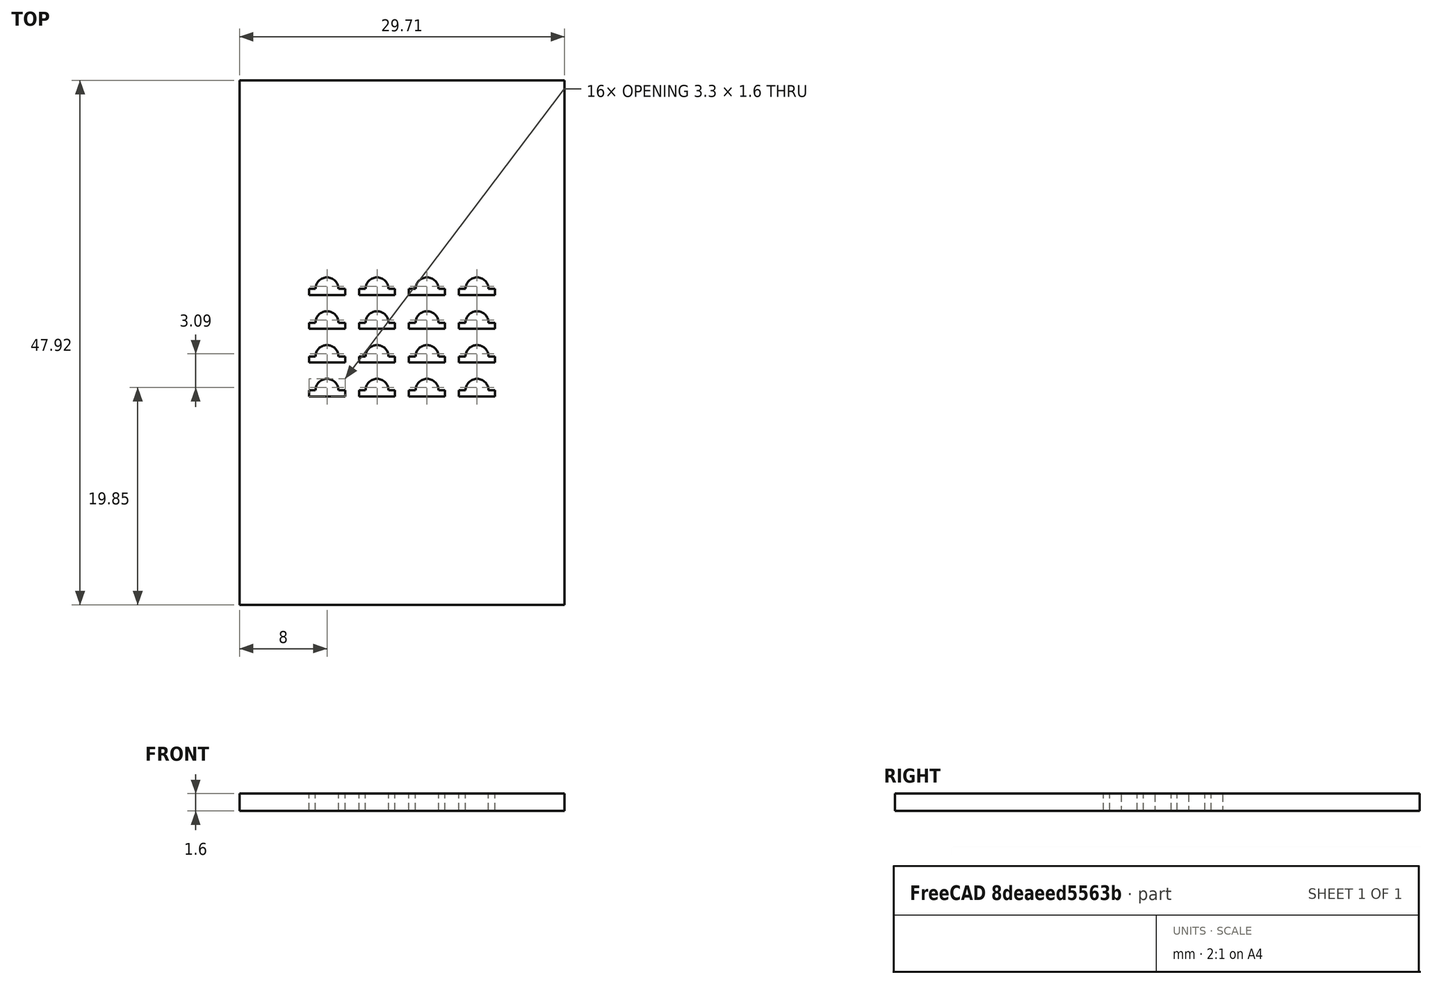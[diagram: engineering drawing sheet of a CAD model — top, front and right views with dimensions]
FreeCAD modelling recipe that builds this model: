
FCSTD DOCUMENT  (FreeCAD 0.18.1R)
Label: Board_Outline_Rev_01
License: All rights reserved
LicenseURL: http://en.wikipedia.org/wiki/All_rights_reserved
objects: Sketcher::SketchObject×1, PartDesign::Pad×1, PartDesign::Body×1, Mesh::Feature×1
note: 4 computed .brp shape members not serialized (recipe doc carries the construction recipe); baked Part::Feature solids carry a one-line shape summary decoded from their .brp

FEATURE [Sketcher::SketchObject] Sketch
  MapMode = 5
  Support = -> [XY_Plane]
  sketch-geometry (116):
    g0: LineSegment StartX=0 StartY=0 StartZ=0 EndX=1.65 EndY=0 EndZ=0
    g1: LineSegment StartX=0 StartY=0 StartZ=0 EndX=-1.65 EndY=0 EndZ=0
    g2: LineSegment StartX=-1.65 StartY=0 StartZ=0 EndX=-1.65 EndY=0.55 EndZ=0
    g3: LineSegment StartX=1.65 StartY=0 StartZ=0 EndX=1.65 EndY=0.55 EndZ=0
    g4: LineSegment StartX=-1.65 StartY=0.55 StartZ=0 EndX=-1.05 EndY=0.55 EndZ=0
    g5: LineSegment StartX=1.65 StartY=0.55 StartZ=0 EndX=1.05 EndY=0.55 EndZ=0
    g6: ArcOfCircle CenterX=0 CenterY=0.55 CenterZ=0 NormalX=0 NormalY=0 NormalZ=1 AngleXU=0 Radius=1.05 StartAngle=0 EndAngle=3.14159
    g7: LineSegment StartX=4.57 StartY=0 StartZ=0 EndX=6.22 EndY=0 EndZ=0
    g8: LineSegment StartX=4.57 StartY=0 StartZ=0 EndX=2.92 EndY=0 EndZ=0
    g9: LineSegment StartX=2.92 StartY=0 StartZ=0 EndX=2.92 EndY=0.55 EndZ=0
    g10: LineSegment StartX=6.22 StartY=0 StartZ=0 EndX=6.22 EndY=0.55 EndZ=0
    g11: LineSegment StartX=2.92 StartY=0.55 StartZ=0 EndX=3.52 EndY=0.55 EndZ=0
    g12: LineSegment StartX=6.22 StartY=0.55 StartZ=0 EndX=5.62 EndY=0.55 EndZ=0
    g13: ArcOfCircle CenterX=4.57 CenterY=0.55 CenterZ=0 NormalX=0 NormalY=0 NormalZ=1 AngleXU=0 Radius=1.05 StartAngle=0 EndAngle=3.14159
    g14: LineSegment StartX=9.14 StartY=0 StartZ=0 EndX=10.79 EndY=0 EndZ=0
    g15: LineSegment StartX=9.14 StartY=0 StartZ=0 EndX=7.49 EndY=0 EndZ=0
    g16: LineSegment StartX=7.49 StartY=0 StartZ=0 EndX=7.49 EndY=0.55 EndZ=0
    g17: LineSegment StartX=10.79 StartY=0 StartZ=0 EndX=10.79 EndY=0.55 EndZ=0
    g18: LineSegment StartX=7.49 StartY=0.55 StartZ=0 EndX=8.09 EndY=0.55 EndZ=0
    g19: LineSegment StartX=10.79 StartY=0.55 StartZ=0 EndX=10.19 EndY=0.55 EndZ=0
    g20: ArcOfCircle CenterX=9.14 CenterY=0.55 CenterZ=0 NormalX=0 NormalY=0 NormalZ=1 AngleXU=0 Radius=1.05 StartAngle=0 EndAngle=3.14159
    g21: LineSegment StartX=13.71 StartY=0 StartZ=0 EndX=15.36 EndY=0 EndZ=0
    g22: LineSegment StartX=13.71 StartY=0 StartZ=0 EndX=12.06 EndY=0 EndZ=0
    g23: LineSegment StartX=12.06 StartY=0 StartZ=0 EndX=12.06 EndY=0.55 EndZ=0
    g24: LineSegment StartX=15.36 StartY=0 StartZ=0 EndX=15.36 EndY=0.55 EndZ=0
    g25: LineSegment StartX=12.06 StartY=0.55 StartZ=0 EndX=12.66 EndY=0.55 EndZ=0
    g26: LineSegment StartX=15.36 StartY=0.55 StartZ=0 EndX=14.76 EndY=0.55 EndZ=0
    g27: ArcOfCircle CenterX=13.71 CenterY=0.55 CenterZ=0 NormalX=0 NormalY=0 NormalZ=1 AngleXU=0 Radius=1.05 StartAngle=0 EndAngle=3.14159
    g28: LineSegment StartX=1e-06 StartY=3.09 StartZ=0 EndX=1.65 EndY=3.09 EndZ=0
    g29: LineSegment StartX=1e-06 StartY=3.09 StartZ=0 EndX=-1.65 EndY=3.09 EndZ=0
    g30: LineSegment StartX=-1.65 StartY=3.09 StartZ=0 EndX=-1.65 EndY=3.64 EndZ=0
    g31: LineSegment StartX=1.65 StartY=3.09 StartZ=0 EndX=1.65 EndY=3.64 EndZ=0
    g32: LineSegment StartX=-1.65 StartY=3.64 StartZ=0 EndX=-1.05 EndY=3.64 EndZ=0
    g33: LineSegment StartX=1.65 StartY=3.64 StartZ=0 EndX=1.05 EndY=3.64 EndZ=0
    g34: ArcOfCircle CenterX=0 CenterY=3.64 CenterZ=0 NormalX=0 NormalY=0 NormalZ=1 AngleXU=0 Radius=1.05 StartAngle=3e-16 EndAngle=3.14159
    g35: LineSegment StartX=4.57 StartY=3.09 StartZ=0 EndX=6.22 EndY=3.09 EndZ=0
    g36: LineSegment StartX=4.57 StartY=3.09 StartZ=0 EndX=2.92 EndY=3.09 EndZ=0
    g37: LineSegment StartX=2.92 StartY=3.09 StartZ=0 EndX=2.92 EndY=3.64 EndZ=0
    g38: LineSegment StartX=6.22 StartY=3.09 StartZ=0 EndX=6.22 EndY=3.64 EndZ=0
    g39: LineSegment StartX=2.92 StartY=3.64 StartZ=0 EndX=3.52 EndY=3.64 EndZ=0
    g40: LineSegment StartX=6.22 StartY=3.64 StartZ=0 EndX=5.62 EndY=3.64 EndZ=0
    g41: ArcOfCircle CenterX=4.57 CenterY=3.64 CenterZ=0 NormalX=0 NormalY=0 NormalZ=1 AngleXU=0 Radius=1.05 StartAngle=1.4e-15 EndAngle=3.14159
    g42: LineSegment StartX=9.14 StartY=3.09 StartZ=0 EndX=10.79 EndY=3.09 EndZ=0
    g43: LineSegment StartX=9.14 StartY=3.09 StartZ=0 EndX=7.49 EndY=3.09 EndZ=0
    g44: LineSegment StartX=7.49 StartY=3.09 StartZ=0 EndX=7.49 EndY=3.64 EndZ=0
    g45: LineSegment StartX=10.79 StartY=3.09 StartZ=0 EndX=10.79 EndY=3.64 EndZ=0
    g46: LineSegment StartX=7.49 StartY=3.64 StartZ=0 EndX=8.09 EndY=3.64 EndZ=0
    g47: LineSegment StartX=10.79 StartY=3.64 StartZ=0 EndX=10.19 EndY=3.64 EndZ=0
    g48: ArcOfCircle CenterX=9.14 CenterY=3.64 CenterZ=0 NormalX=0 NormalY=0 NormalZ=1 AngleXU=0 Radius=1.05 StartAngle=0 EndAngle=3.14159
    g49: LineSegment StartX=13.71 StartY=3.09 StartZ=0 EndX=15.36 EndY=3.09 EndZ=0
    g50: LineSegment StartX=13.71 StartY=3.09 StartZ=0 EndX=12.06 EndY=3.09 EndZ=0
    g51: LineSegment StartX=12.06 StartY=3.09 StartZ=0 EndX=12.06 EndY=3.64 EndZ=0
    g52: LineSegment StartX=15.36 StartY=3.09 StartZ=0 EndX=15.36 EndY=3.64 EndZ=0
    g53: LineSegment StartX=12.06 StartY=3.64 StartZ=0 EndX=12.66 EndY=3.64 EndZ=0
    g54: LineSegment StartX=15.36 StartY=3.64 StartZ=0 EndX=14.76 EndY=3.64 EndZ=0
    g55: ArcOfCircle CenterX=13.71 CenterY=3.64 CenterZ=0 NormalX=0 NormalY=0 NormalZ=1 AngleXU=0 Radius=1.05 StartAngle=5.7e-15 EndAngle=3.14159
    g56: LineSegment StartX=0 StartY=6.18 StartZ=0 EndX=1.65 EndY=6.18 EndZ=0
    g57: LineSegment StartX=0 StartY=6.18 StartZ=0 EndX=-1.65 EndY=6.18 EndZ=0
    g58: LineSegment StartX=-1.65 StartY=6.18 StartZ=0 EndX=-1.65 EndY=6.73 EndZ=0
    g59: LineSegment StartX=1.65 StartY=6.18 StartZ=0 EndX=1.65 EndY=6.73 EndZ=0
    g60: LineSegment StartX=-1.65 StartY=6.73 StartZ=0 EndX=-1.05 EndY=6.73 EndZ=0
    g61: LineSegment StartX=1.65 StartY=6.73 StartZ=0 EndX=1.05 EndY=6.73 EndZ=0
    g62: ArcOfCircle CenterX=0 CenterY=6.73 CenterZ=0 NormalX=0 NormalY=0 NormalZ=1 AngleXU=0 Radius=1.05 StartAngle=7e-16 EndAngle=3.14159
    g63: LineSegment StartX=4.57 StartY=6.18 StartZ=0 EndX=6.22 EndY=6.18 EndZ=0
    g64: LineSegment StartX=4.57 StartY=6.18 StartZ=0 EndX=2.92 EndY=6.18 EndZ=0
    g65: LineSegment StartX=2.92 StartY=6.18 StartZ=0 EndX=2.92 EndY=6.73 EndZ=0
    g66: LineSegment StartX=6.22 StartY=6.18 StartZ=0 EndX=6.22 EndY=6.73 EndZ=0
    g67: LineSegment StartX=2.92 StartY=6.73 StartZ=0 EndX=3.52 EndY=6.73 EndZ=0
    g68: LineSegment StartX=6.22 StartY=6.73 StartZ=0 EndX=5.62 EndY=6.73 EndZ=0
    g69: ArcOfCircle CenterX=4.57 CenterY=6.73 CenterZ=0 NormalX=0 NormalY=0 NormalZ=1 AngleXU=0 Radius=1.05 StartAngle=-9e-16 EndAngle=3.14159
    g70: LineSegment StartX=9.14 StartY=6.18 StartZ=0 EndX=10.79 EndY=6.18 EndZ=0
    g71: LineSegment StartX=9.14 StartY=6.18 StartZ=0 EndX=7.49 EndY=6.18 EndZ=0
    g72: LineSegment StartX=7.49 StartY=6.18 StartZ=0 EndX=7.49 EndY=6.73 EndZ=0
    g73: LineSegment StartX=10.79 StartY=6.18 StartZ=0 EndX=10.79 EndY=6.73 EndZ=0
    g74: LineSegment StartX=7.49 StartY=6.73 StartZ=0 EndX=8.09 EndY=6.73 EndZ=0
    g75: LineSegment StartX=10.79 StartY=6.73 StartZ=0 EndX=10.19 EndY=6.73 EndZ=0
    g76: ArcOfCircle CenterX=9.14 CenterY=6.73 CenterZ=0 NormalX=0 NormalY=0 NormalZ=1 AngleXU=0 Radius=1.05 StartAngle=4.3e-15 EndAngle=3.14159
    g77: LineSegment StartX=13.71 StartY=6.18 StartZ=0 EndX=15.36 EndY=6.18 EndZ=0
    g78: LineSegment StartX=13.71 StartY=6.18 StartZ=0 EndX=12.06 EndY=6.18 EndZ=0
    g79: LineSegment StartX=12.06 StartY=6.18 StartZ=0 EndX=12.06 EndY=6.73 EndZ=0
    g80: LineSegment StartX=15.36 StartY=6.18 StartZ=0 EndX=15.36 EndY=6.73 EndZ=0
    g81: LineSegment StartX=12.06 StartY=6.73 StartZ=0 EndX=12.66 EndY=6.73 EndZ=0
    g82: LineSegment StartX=15.36 StartY=6.73 StartZ=0 EndX=14.76 EndY=6.73 EndZ=0
    g83: ArcOfCircle CenterX=13.71 CenterY=6.73 CenterZ=0 NormalX=0 NormalY=0 NormalZ=1 AngleXU=0 Radius=1.05 StartAngle=1.2e-15 EndAngle=3.14159
    g84: LineSegment StartX=1e-06 StartY=9.27 StartZ=0 EndX=1.65 EndY=9.27 EndZ=0
    g85: LineSegment StartX=1e-06 StartY=9.27 StartZ=0 EndX=-1.65 EndY=9.27 EndZ=0
    g86: LineSegment StartX=-1.65 StartY=9.27 StartZ=0 EndX=-1.65 EndY=9.82 EndZ=0
    g87: LineSegment StartX=1.65 StartY=9.27 StartZ=0 EndX=1.65 EndY=9.82 EndZ=0
    g88: LineSegment StartX=-1.65 StartY=9.82 StartZ=0 EndX=-1.05 EndY=9.82 EndZ=0
    g89: LineSegment StartX=1.65 StartY=9.82 StartZ=0 EndX=1.05 EndY=9.82 EndZ=0
    g90: ArcOfCircle CenterX=0 CenterY=9.82 CenterZ=0 NormalX=0 NormalY=0 NormalZ=1 AngleXU=0 Radius=1.05 StartAngle=-1.8e-15 EndAngle=3.14159
    g91: LineSegment StartX=4.57 StartY=9.27 StartZ=0 EndX=6.22 EndY=9.27 EndZ=0
    g92: LineSegment StartX=4.57 StartY=9.27 StartZ=0 EndX=2.92 EndY=9.27 EndZ=0
    g93: LineSegment StartX=2.92 StartY=9.27 StartZ=0 EndX=2.92 EndY=9.82 EndZ=0
    g94: LineSegment StartX=6.22 StartY=9.27 StartZ=0 EndX=6.22 EndY=9.82 EndZ=0
    g95: LineSegment StartX=2.92 StartY=9.82 StartZ=0 EndX=3.52 EndY=9.82 EndZ=0
    g96: LineSegment StartX=6.22 StartY=9.82 StartZ=0 EndX=5.62 EndY=9.82 EndZ=0
    g97: ArcOfCircle CenterX=4.57 CenterY=9.82 CenterZ=0 NormalX=0 NormalY=0 NormalZ=1 AngleXU=0 Radius=1.05 StartAngle=6e-16 EndAngle=3.14159
    g98: LineSegment StartX=9.14 StartY=9.27 StartZ=0 EndX=10.79 EndY=9.27 EndZ=0
    g99: LineSegment StartX=9.14 StartY=9.27 StartZ=0 EndX=7.49 EndY=9.27 EndZ=0
    g100: LineSegment StartX=7.49 StartY=9.27 StartZ=0 EndX=7.49 EndY=9.82 EndZ=0
    g101: LineSegment StartX=10.79 StartY=9.27 StartZ=0 EndX=10.79 EndY=9.82 EndZ=0
    g102: LineSegment StartX=7.49 StartY=9.82 StartZ=0 EndX=8.09 EndY=9.82 EndZ=0
    g103: LineSegment StartX=10.79 StartY=9.82 StartZ=0 EndX=10.19 EndY=9.82 EndZ=0
    g104: ArcOfCircle CenterX=9.14 CenterY=9.82 CenterZ=0 NormalX=0 NormalY=0 NormalZ=1 AngleXU=0 Radius=1.05 StartAngle=-1.8e-15 EndAngle=3.14159
    g105: LineSegment StartX=13.71 StartY=9.27 StartZ=0 EndX=15.36 EndY=9.27 EndZ=0
    g106: LineSegment StartX=13.71 StartY=9.27 StartZ=0 EndX=12.06 EndY=9.27 EndZ=0
    g107: LineSegment StartX=12.06 StartY=9.27 StartZ=0 EndX=12.06 EndY=9.82 EndZ=0
    g108: LineSegment StartX=15.36 StartY=9.27 StartZ=0 EndX=15.36 EndY=9.82 EndZ=0
    g109: LineSegment StartX=12.06 StartY=9.82 StartZ=0 EndX=12.66 EndY=9.82 EndZ=0
    g110: LineSegment StartX=15.36 StartY=9.82 StartZ=0 EndX=14.76 EndY=9.82 EndZ=0
    g111: ArcOfCircle CenterX=13.71 CenterY=9.82 CenterZ=0 NormalX=0 NormalY=0 NormalZ=1 AngleXU=0 Radius=1.05 StartAngle=-8.9e-15 EndAngle=3.14159
    g112: LineSegment StartX=-8 StartY=-19.05 StartZ=0 EndX=21.71 EndY=-19.05 EndZ=0
    g113: LineSegment StartX=21.71 StartY=-19.05 StartZ=0 EndX=21.71 EndY=28.87 EndZ=0
    g114: LineSegment StartX=21.71 StartY=28.87 StartZ=0 EndX=-8 EndY=28.87 EndZ=0
    g115: LineSegment StartX=-8 StartY=28.87 StartZ=0 EndX=-8 EndY=-19.05 EndZ=0
  constraints (363):
    c: Coincident(g0,g-1)
    c: PointOnObject(g0,g-1)
    c: Coincident(g1,g0)
    c: PointOnObject(g1,g-1)
    c: Coincident(g2,g1)
    c: Vertical(g2)
    c: Coincident(g3,g0)
    c: Vertical(g3)
    c: Coincident(g4,g2)
    c: Horizontal(g4)
    c: Coincident(g5,g3)
    c: Horizontal(g5)
    c: Coincident(g6,g4)
    c: Coincident(g6,g5)
    c: DistanceY(g3,g3) = 0.55
    c: DistanceY(g2,g2) = 0.55
    c: Distance(g6,g0) = 0.55
    c: PointOnObject(g6,g-2)
    c: Distance(g1,g0) = 3.3
    c: Radius(g6) = 1.05
    c: Distance(g0) = 1.65
    c: Coincident(g8,g7)
    c: Coincident(g9,g8)
    c: Vertical(g9)
    c: Coincident(g10,g7)
    c: Vertical(g10)
    c: Coincident(g11,g9)
    c: Horizontal(g11)
    c: Coincident(g12,g10)
    c: Horizontal(g12)
    c: Coincident(g13,g11)
    c: Coincident(g13,g12)
    c: Equal(g3,g10) = 0.55
    c: Equal(g2,g9) = 0.55
    c: Distance(g13,g7) = 0.55
    c: Distance(g8,g7) = 3.3
    c: Equal(g6,g13) = 1.05
    c: Equal(g0,g7) = 1.65
    c: Coincident(g15,g14)
    c: Coincident(g16,g15)
    c: Vertical(g16)
    c: Coincident(g17,g14)
    c: Vertical(g17)
    c: Coincident(g18,g16)
    c: Horizontal(g18)
    c: Coincident(g19,g17)
    c: Horizontal(g19)
    c: Coincident(g20,g18)
    c: Coincident(g20,g19)
    c: Equal(g3,g17) = 0.55
    c: Equal(g2,g16) = 0.55
    c: Distance(g20,g14) = 0.55
    c: Distance(g15,g14) = 3.3
    c: Equal(g6,g20) = 1.05
    c: Equal(g0,g14) = 1.65
    c: Coincident(g22,g21)
    c: Coincident(g23,g22)
    c: Vertical(g23)
    c: Coincident(g24,g21)
    c: Vertical(g24)
    c: Coincident(g25,g23)
    c: Horizontal(g25)
    c: Coincident(g26,g24)
    c: Horizontal(g26)
    c: Coincident(g27,g25)
    c: Coincident(g27,g26)
    c: Equal(g3,g24) = 0.55
    c: Equal(g2,g23) = 0.55
    c: Distance(g27,g21) = 0.55
    c: Distance(g22,g21) = 3.3
    c: Equal(g6,g27) = 1.05
    c: Equal(g0,g21) = 1.65
    c: PointOnObject(g8,g-1)
    c: PointOnObject(g7,g-1)
    c: PointOnObject(g7,g-1)
    c: Distance(g0,g8) = 1.27
    c: DistanceX(g11,g11) = 0.6
    c: Distance(g18) = 0.599999
    c: PointOnObject(g15,g-1)
    c: PointOnObject(g14,g-1)
    c: PointOnObject(g14,g-1)
    c: Distance(g10,g16) = 1.27
    c: Distance(g25) = 0.599999
    c: PointOnObject(g22,g-1)
    c: PointOnObject(g21,g-1)
    c: PointOnObject(g21,g-1)
    c: Distance(g17,g23) = 1.27
    c: Coincident(g29,g28)
    c: Coincident(g30,g29)
    c: Vertical(g30)
    c: Coincident(g31,g28)
    c: Vertical(g31)
    c: Coincident(g32,g30)
    c: Horizontal(g32)
    c: Coincident(g33,g31)
    c: Horizontal(g33)
    c: Coincident(g34,g32)
    c: Coincident(g34,g33)
    c: Equal(g3,g31) = 0.55
    c: Equal(g2,g30) = 0.55
    c: Distance(g34,g28) = 0.55
    c: Distance(g29,g28) = 3.3
    c: Equal(g6,g34) = 1.05
    c: Equal(g0,g28) = 1.65
    c: Coincident(g36,g35)
    c: Coincident(g37,g36)
    c: Vertical(g37)
    c: Coincident(g38,g35)
    c: Vertical(g38)
    c: Coincident(g39,g37)
    c: Horizontal(g39)
    c: Coincident(g40,g38)
    c: Horizontal(g40)
    c: Coincident(g41,g39)
    c: Coincident(g41,g40)
    c: Equal(g31,g38) = 0.55
    c: Equal(g30,g37) = 0.55
    c: Distance(g41,g35) = 0.55
    c: Distance(g36,g35) = 3.3
    c: Equal(g34,g41) = 1.05
    c: Equal(g28,g35) = 1.65
    c: Coincident(g43,g42)
    c: Coincident(g44,g43)
    c: Vertical(g44)
    c: Coincident(g45,g42)
    c: Vertical(g45)
    c: Coincident(g46,g44)
    c: Horizontal(g46)
    c: Coincident(g47,g45)
    c: Horizontal(g47)
    c: Coincident(g48,g46)
    c: Coincident(g48,g47)
    c: Equal(g31,g45) = 0.55
    c: Equal(g30,g44) = 0.55
    c: Distance(g48,g42) = 0.55
    c: Distance(g43,g42) = 3.3
    c: Equal(g34,g48) = 1.05
    c: Equal(g28,g42) = 1.65
    c: Coincident(g50,g49)
    c: Coincident(g51,g50)
    c: Vertical(g51)
    c: Coincident(g52,g49)
    c: Vertical(g52)
    c: Coincident(g53,g51)
    c: Horizontal(g53)
    c: Coincident(g54,g52)
    c: Horizontal(g54)
    c: Coincident(g55,g53)
    c: Coincident(g55,g54)
    c: Equal(g31,g52) = 0.55
    c: Equal(g30,g51) = 0.55
    c: Distance(g55,g49) = 0.55
    c: Distance(g50,g49) = 3.3
    c: Equal(g34,g55) = 1.05
    c: Equal(g28,g49) = 1.65
    c: Distance(g28,g36) = 1.27
    c: Equal(g11,g39) = 0.6
    c: Equal(g18,g46) = 0.599999
    c: Distance(g38,g44) = 1.27
    c: Equal(g25,g53) = 0.599999
    c: Distance(g45,g51) = 1.27
    c: Horizontal(g50)
    c: Horizontal(g49)
    c: Horizontal(g42)
    c: Horizontal(g43)
    c: Horizontal(g35)
    c: Horizontal(g36)
    c: Horizontal(g28)
    c: Horizontal(g29)
    c: Distance(g3,g28) = 2.54
    c: Distance(g35,g10) = 2.54
    c: Distance(g42,g17) = 2.54
    c: Distance(g49,g24) = 2.54
    c: Distance(g32) = 0.599999
    c: PointOnObject(g34,g-2)
    c: Coincident(g57,g56)
    c: Coincident(g58,g57)
    c: Vertical(g58)
    c: Coincident(g59,g56)
    c: Vertical(g59)
    c: Coincident(g60,g58)
    c: Horizontal(g60)
    c: Coincident(g61,g59)
    c: Horizontal(g61)
    c: Coincident(g62,g60)
    c: Coincident(g62,g61)
    c: Equal(g3,g59) = 0.55
    c: Equal(g2,g58) = 0.55
    c: Distance(g62,g56) = 0.55
    c: Distance(g57,g56) = 3.3
    c: Equal(g6,g62) = 1.05
    c: Equal(g0,g56) = 1.65
    c: Coincident(g64,g63)
    c: Coincident(g65,g64)
    c: Vertical(g65)
    c: Coincident(g66,g63)
    c: Vertical(g66)
    c: Coincident(g67,g65)
    c: Horizontal(g67)
    c: Coincident(g68,g66)
    c: Horizontal(g68)
    c: Coincident(g69,g67)
    c: Coincident(g69,g68)
    c: Equal(g59,g66) = 0.55
    c: Equal(g58,g65) = 0.55
    c: Distance(g69,g63) = 0.55
    c: Distance(g64,g63) = 3.3
    c: Equal(g62,g69) = 1.05
    c: Equal(g56,g63) = 1.65
    c: Coincident(g71,g70)
    c: Coincident(g72,g71)
    c: Vertical(g72)
    c: Coincident(g73,g70)
    c: Vertical(g73)
    c: Coincident(g74,g72)
    c: Horizontal(g74)
    c: Coincident(g75,g73)
    c: Horizontal(g75)
    c: Coincident(g76,g74)
    c: Coincident(g76,g75)
    c: Equal(g59,g73) = 0.55
    c: Equal(g58,g72) = 0.55
    c: Distance(g76,g70) = 0.55
    c: Distance(g71,g70) = 3.3
    c: Equal(g62,g76) = 1.05
    c: Equal(g56,g70) = 1.65
    c: Coincident(g78,g77)
    c: Coincident(g79,g78)
    c: Vertical(g79)
    c: Coincident(g80,g77)
    c: Vertical(g80)
    c: Coincident(g81,g79)
    c: Horizontal(g81)
    c: Coincident(g82,g80)
    c: Horizontal(g82)
    c: Coincident(g83,g81)
    c: Coincident(g83,g82)
    c: Equal(g59,g80) = 0.55
    c: Equal(g58,g79) = 0.55
    c: Distance(g83,g77) = 0.55
    c: Distance(g78,g77) = 3.3
    c: Equal(g62,g83) = 1.05
    c: Equal(g56,g77) = 1.65
    c: Distance(g56,g64) = 1.27
    c: Equal(g11,g67) = 0.6
    c: Equal(g18,g74) = 0.599999
    c: Distance(g66,g72) = 1.27
    c: Equal(g25,g81) = 0.599999
    c: Distance(g73,g79) = 1.27
    c: Coincident(g85,g84)
    c: Coincident(g86,g85)
    c: Vertical(g86)
    c: Coincident(g87,g84)
    c: Vertical(g87)
    c: Coincident(g88,g86)
    c: Horizontal(g88)
    c: Coincident(g89,g87)
    c: Horizontal(g89)
    c: Coincident(g90,g88)
    c: Coincident(g90,g89)
    c: Equal(g59,g87) = 0.55
    c: Equal(g58,g86) = 0.55
    c: Distance(g90,g84) = 0.55
    c: Distance(g85,g84) = 3.3
    c: Equal(g62,g90) = 1.05
    c: Equal(g56,g84) = 1.65
    c: Coincident(g92,g91)
    c: Coincident(g93,g92)
    c: Vertical(g93)
    c: Coincident(g94,g91)
    c: Vertical(g94)
    c: Coincident(g95,g93)
    c: Horizontal(g95)
    c: Coincident(g96,g94)
    c: Horizontal(g96)
    c: Coincident(g97,g95)
    c: Coincident(g97,g96)
    c: Equal(g87,g94) = 0.55
    c: Equal(g86,g93) = 0.55
    c: Distance(g97,g91) = 0.55
    c: Distance(g92,g91) = 3.3
    c: Equal(g90,g97) = 1.05
    c: Equal(g84,g91) = 1.65
    c: Coincident(g99,g98)
    c: Coincident(g100,g99)
    c: Vertical(g100)
    c: Coincident(g101,g98)
    c: Vertical(g101)
    c: Coincident(g102,g100)
    c: Horizontal(g102)
    c: Coincident(g103,g101)
    c: Horizontal(g103)
    c: Coincident(g104,g102)
    c: Coincident(g104,g103)
    c: Equal(g87,g101) = 0.55
    c: Equal(g86,g100) = 0.55
    c: Distance(g104,g98) = 0.55
    c: Distance(g99,g98) = 3.3
    c: Equal(g90,g104) = 1.05
    c: Equal(g84,g98) = 1.65
    c: Coincident(g106,g105)
    c: Coincident(g107,g106)
    c: Vertical(g107)
    c: Coincident(g108,g105)
    c: Vertical(g108)
    c: Coincident(g109,g107)
    c: Horizontal(g109)
    c: Coincident(g110,g108)
    c: Horizontal(g110)
    c: Coincident(g111,g109)
    c: Coincident(g111,g110)
    c: Equal(g87,g108) = 0.55
    c: Equal(g86,g107) = 0.55
    c: Distance(g111,g105) = 0.55
    c: Distance(g106,g105) = 3.3
    c: Equal(g90,g111) = 1.05
    c: Equal(g84,g105) = 1.65
    c: Distance(g84,g92) = 1.27
    c: Equal(g67,g95) = 0.6
    c: Equal(g74,g102) = 0.599999
    c: Distance(g94,g100) = 1.27
    c: Equal(g81,g109) = 0.599999
    c: Distance(g101,g107) = 1.27
    c: Horizontal(g106)
    c: Horizontal(g105)
    c: Horizontal(g98)
    c: Horizontal(g99)
    c: Horizontal(g91)
    c: Horizontal(g92)
    c: Horizontal(g84)
    c: Horizontal(g85)
    c: Distance(g59,g84) = 2.54
    c: Distance(g91,g66) = 2.54
    c: Distance(g98,g73) = 2.54
    c: Distance(g105,g80) = 2.54
    c: Equal(g32,g88) = 0.599999
    c: PointOnObject(g62,g-2)
    c: PointOnObject(g56,g-2)
    c: Horizontal(g57)
    c: Horizontal(g56)
    c: Horizontal(g64)
    c: Horizontal(g63)
    c: Horizontal(g71)
    c: Horizontal(g70)
    c: Horizontal(g78)
    c: Horizontal(g77)
    c: Distance(g56,g31) = 2.54
    c: Distance(g63,g38) = 2.54
    c: Distance(g45,g70) = 2.54
    c: Distance(g52,g77) = 2.54
    c: PointOnObject(g90,g-2)
    c: Coincident(g112,g113)
    c: Coincident(g113,g114)
    c: Coincident(g114,g115)
    c: Coincident(g115,g112)
    c: Horizontal(g112)
    c: Horizontal(g114)
    c: Vertical(g113)
    c: Vertical(g115)
    c: Distance(g0,g112) = 19.05
    c: Distance(g21,g113) = 6.35
    c: Distance(g87,g114) = 19.05
    c: Distance(g1,g115) = 6.35
FEATURE [PartDesign::Pad] Pad
  Length = 1.6002
  Length2 = 100.076
  Profile = -> Sketch
  Type = 0
FEATURE [PartDesign::Body] Body
  Group = -> [Sketch,Pad]
  Origin = -> Origin
  Tip = -> Pad
FEATURE [Mesh::Feature] Mesh  label="Pad (Meshed)"
